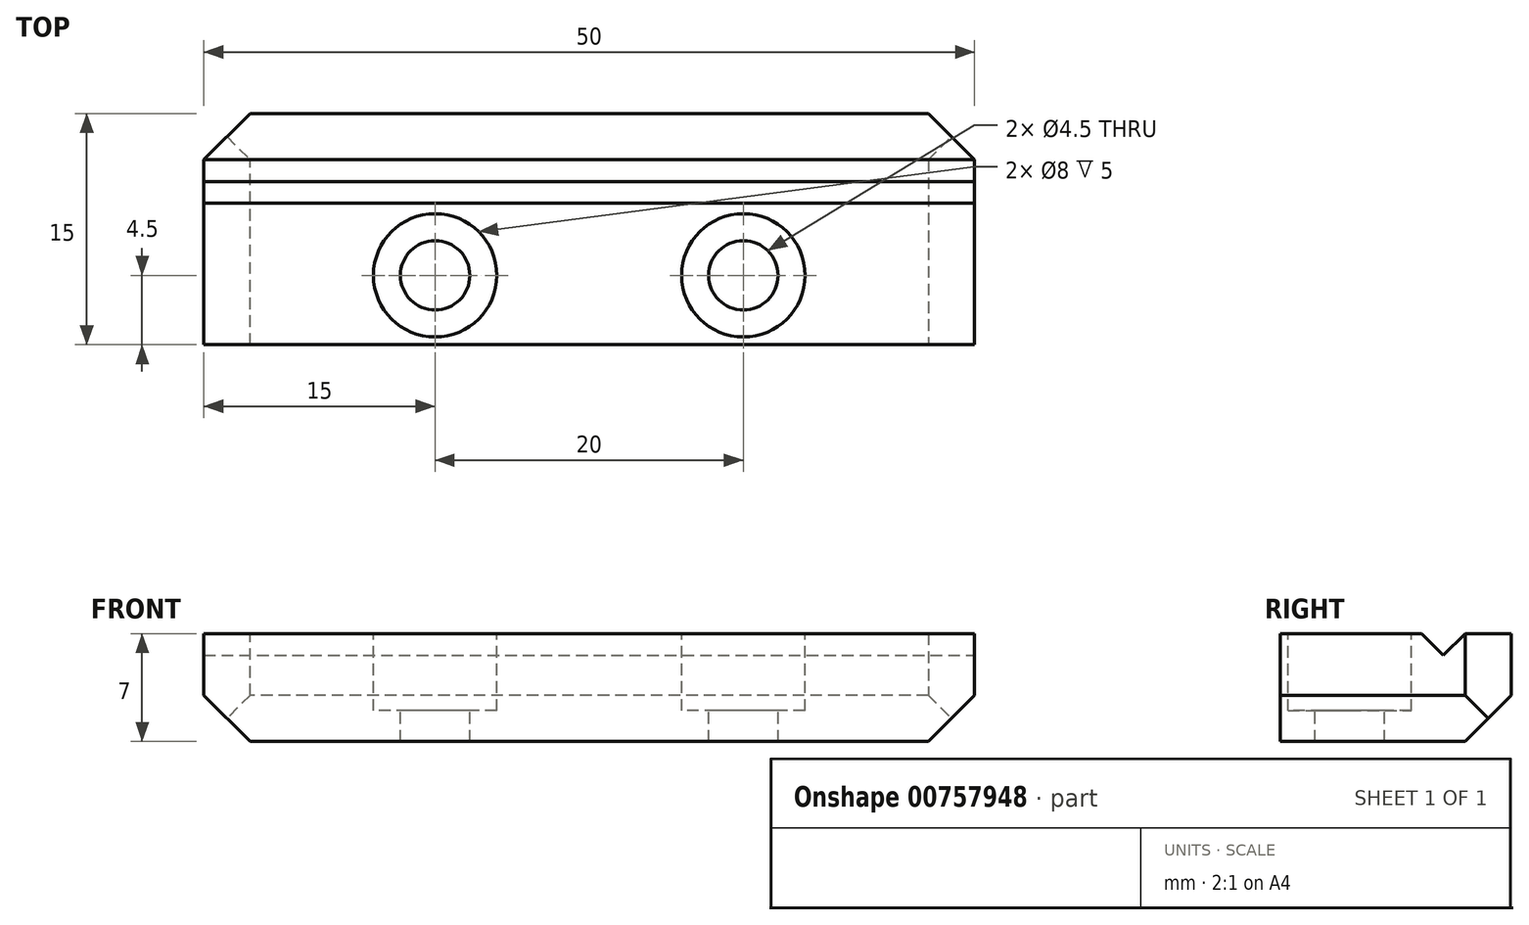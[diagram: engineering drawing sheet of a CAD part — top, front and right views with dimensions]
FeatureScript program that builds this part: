
annotation { "Feature Type Name" : "Feature", "Feature Type Description" : "" }
export const myFeature = defineFeature(function(context is Context, id is Id, definition is map)
    precondition{}
    {
        {
            var Q0;
            Q0=qCreatedBy(makeId("Top.planeOp"),FACE);
            var sketch = newSketch(context, id + "F0", { "sketchPlane" : qUnion([Q0])});
            skLineSegment(sketch, "E0.bottom", {"start": v(20, -5) * mm, "end": v(-20, -5) * mm});
            skPoint(sketch, "E0.middle", {"position": v(0, 0) * mm});
            skLineSegment(sketch, "E1.top", {"start": v(-20, 10) * mm, "end": v(20, 10) * mm});
            skLineSegment(sketch, "E2.bottom", {"start": v(-20, 10) * mm, "end": v(-25, 10) * mm});
            skLineSegment(sketch, "E2.top", {"start": v(-20, -5) * mm, "end": v(-25, -5) * mm});
            skLineSegment(sketch, "E2.right", {"start": v(-25, 10) * mm, "end": v(-25, -5) * mm});
            skLineSegment(sketch, "E3.MirrorCS", {"start": v(25, 10) * mm, "end": v(25, -5) * mm});
            skLineSegment(sketch, "E4.MirrorCS", {"start": v(20, 10) * mm, "end": v(25, 10) * mm});
            skLineSegment(sketch, "E5.MirrorCS", {"start": v(20, -5) * mm, "end": v(25, -5) * mm});
            skSolve(sketch);
        }
        {
            var Q0;
            Q0=makeQuery(id+"F0.imprint","IMPRINT",FACE,{"disambiguationData":[TD([[makeQuery(id+"F0.imprint","IMPRINT",EDGE,{"derivedFrom":sQuery(id+"F0.wireOp",EDGE,"E0.bottom")}),-1.0]])]});
            extrude(context, id + "F1", {"entities" : qUnion([Q0]), "depth" : 7 * mm, "offsetDistance" : 25 * mm});
        }
        {
            var Q0;
            Q0=makeQuery(id+"F1.opExtrude","CAP_FACE",FACE,{"disambiguationData":[OSD([sQuery(id+"F0.wireOp",EDGE,"E0.bottom"),sQuery(id+"F0.wireOp",EDGE,"E0.top"),sQuery(id+"F0.wireOp",EDGE,"E0.left"),sQuery(id+"F0.wireOp",EDGE,"E0.right")])],"isStart":false});
            var sketch = newSketch(context, id + "F2", { "sketchPlane" : qUnion([Q0])});
            skPoint(sketch, "E6", {"position": v(-10, -0.5) * mm});
            skPoint(sketch, "E7.MirrorP", {"position": v(10, -0.5) * mm});
            skSolve(sketch);
        }
        {
            var Q0;
            Q0=sQuery(id+"F2.wireOp",VERTEX,"E6");
            var Q1;
            Q1=sQuery(id+"F2.wireOp",VERTEX,"E7.MirrorP");
            var Q2;
            Q2=makeQuery(id+"F1.opExtrude","SWEPT_BODY",BODY,{"disambiguationData":[OSD([sQuery(id+"F0.wireOp",EDGE,"E0.bottom"),sQuery(id+"F0.wireOp",EDGE,"E0.top"),sQuery(id+"F0.wireOp",EDGE,"E0.left"),sQuery(id+"F0.wireOp",EDGE,"E0.right")])]});
            hole(context, id + "F3", {"style" : HoleStyle.C_BORE, "endStyle" : HoleEndStyle.THROUGH, "holeDiameter" : 4.5 * mm, "cBoreDiameter" : 8 * mm, "cBoreDepth" : 5 * mm, "majorDiameter" : 5 * mm, "isTappedThrough" : true, "tappedDepth" : 6 * mm, "tapClearance" : 3, "locations" : qUnion([Q0, Q1]), "scope" : qUnion([Q2])});
        }
        {
            var Q0;
            Q0=makeQuery(id+"F1.opExtrude","SWEPT_EDGE",EDGE,{"disambiguationData":[OSD([sQuery(id+"F0.wireOp",EDGE,"E2.bottom"),sQuery(id+"F0.wireOp",EDGE,"E2.right")])]});
            var Q1;
            Q1=makeQuery(id+"F1.opExtrude","SWEPT_EDGE",EDGE,{"disambiguationData":[OSD([sQuery(id+"F0.wireOp",EDGE,"E3.MirrorCS"),sQuery(id+"F0.wireOp",EDGE,"E4.MirrorCS")])]});
            chamfer(context, id + "F4", {"entities" : qUnion([Q0, Q1]), "width" : 3 * mm, "tangentPropagation" : true});
        }
        {
            var Q0;
            Q0=makeQuery(id+"F1.opExtrude","CAP_EDGE",EDGE,{"disambiguationData":[OSD([sQuery(id+"F0.wireOp",EDGE,"E1.top"),sQuery(id+"F0.wireOp",EDGE,"E2.bottom"),sQuery(id+"F0.wireOp",EDGE,"E4.MirrorCS")])],"isStart":true});
            var Q1;
            Q1=makeQuery(id+"F1.opExtrude","CAP_EDGE",EDGE,{"disambiguationData":[OSD([sQuery(id+"F0.wireOp",EDGE,"E3.MirrorCS")])],"isStart":true});
            var Q2;
            Q2=makeQuery(id+"F1.opExtrude","CAP_EDGE",EDGE,{"disambiguationData":[OSD([sQuery(id+"F0.wireOp",EDGE,"E2.right")])],"isStart":true});
            chamfer(context, id + "F5", {"entities" : qUnion([Q0, Q1, Q2]), "width" : 3 * mm, "tangentPropagation" : true});
        }
        {
            var Q0;
            Q0=makeQuery(id+"F1.opExtrude","SWEPT_FACE",FACE,{"disambiguationData":[OSD([sQuery(id+"F0.wireOp",EDGE,"E3.MirrorCS")])]});
            var sketch = newSketch(context, id + "F6", { "sketchPlane" : qUnion([Q0])});
            skLineSegment(sketch, "E8", {"start": v(7, 7) * mm, "end": v(5.59, 5.59) * mm});
            skLineSegment(sketch, "E9", {"start": v(5.59, 5.59) * mm, "end": v(4.17, 7) * mm});
            skSolve(sketch);
        }
        {
            var Q0;
            {var subQ0=sQuery(id+"F6.wireOp",EDGE,"E8");Q0=makeQuery(id+"F6.imprint","IMPRINT",FACE,{"disambiguationData":[TD([[makeQuery(id+"F6.imprint","IMPRINT",EDGE,{"derivedFrom":subQ0}),-1.0]])]});}
            extrude(context, id + "F7", {"entities" : qUnion([Q0]), "operationType" : NewBodyOperationType.REMOVE, "oppositeDirection" : true, "depth" : 50 * mm, "offsetDistance" : 25 * mm});
        }
    });
